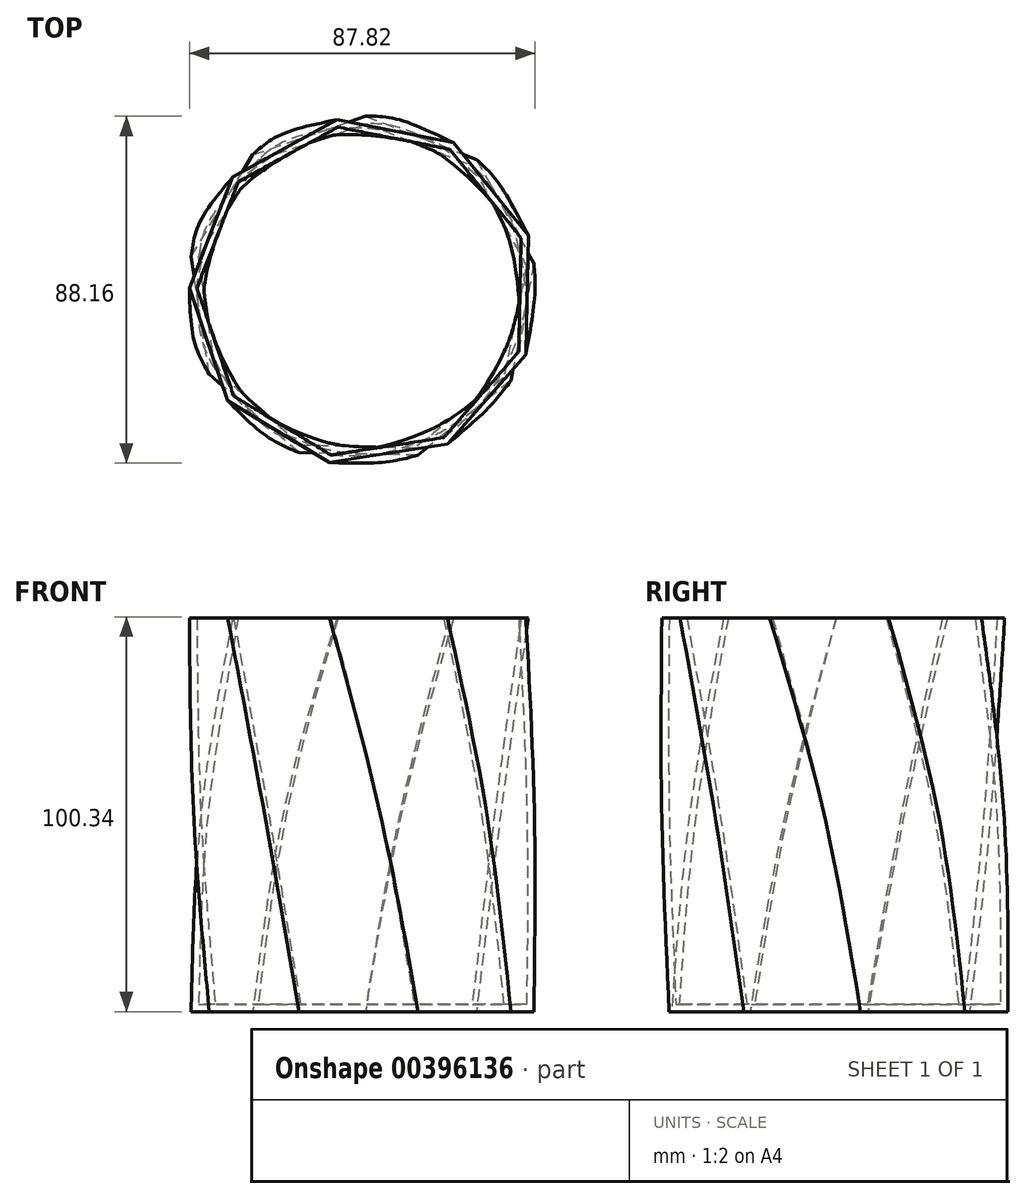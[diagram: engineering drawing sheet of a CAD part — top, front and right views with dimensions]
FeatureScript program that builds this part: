
annotation { "Feature Type Name" : "Feature", "Feature Type Description" : "" }
export const myFeature = defineFeature(function(context is Context, id is Id, definition is map)
    precondition{}
    {
        {
            var Q0;
            Q0=qCreatedBy(makeId("Top.planeOp"),FACE);
            var sketch = newSketch(context, id + "F0", { "sketchPlane" : qUnion([Q0])});
            skCircle(sketch, "E0.cCircle", {"center": v(0, 0) * mm, "radius": 41.56 * mm, "construction": true});
            skLineSegment(sketch, "E0.0", {"start": v(43.7, 6.78) * mm, "end": v(37.84, -22.9) * mm});
            skLineSegment(sketch, "E0.1", {"start": v(37.84, -22.9) * mm, "end": v(14.26, -41.87) * mm});
            skLineSegment(sketch, "E0.2", {"start": v(14.26, -41.87) * mm, "end": v(-15.98, -41.24) * mm});
            skLineSegment(sketch, "E0.3", {"start": v(-15.98, -41.24) * mm, "end": v(-38.75, -21.32) * mm});
            skLineSegment(sketch, "E0.4", {"start": v(-38.75, -21.32) * mm, "end": v(-43.39, 8.58) * mm});
            skLineSegment(sketch, "E0.5", {"start": v(-43.39, 8.58) * mm, "end": v(-27.72, 34.46) * mm});
            skLineSegment(sketch, "E0.6", {"start": v(-27.72, 34.46) * mm, "end": v(0.92, 44.22) * mm});
            skLineSegment(sketch, "E0.7", {"start": v(0.92, 44.22) * mm, "end": v(29.12, 33.29) * mm});
            skLineSegment(sketch, "E0.8", {"start": v(29.12, 33.29) * mm, "end": v(43.7, 6.78) * mm});
            skPoint(sketch, "E0.0.midPoint", {"position": v(40.77, -8.06) * mm});
            skSolve(sketch);
        }
        {
            var Q0;
            Q0=qCreatedBy(makeId("Top.planeOp"),FACE);
            cPlane(context, id + "F1", {"entities" : qUnion([Q0]), "cplaneType" : CPlaneType.OFFSET, "offset" : 50 * mm, "width" : 152.4 * mm, "height" : 152.4 * mm});
        }
        {
            var Q0;
            Q0=qCreatedBy(makeId("Top.planeOp"),FACE);
            cPlane(context, id + "F2", {"entities" : qUnion([Q0]), "cplaneType" : CPlaneType.OFFSET, "offset" : 100 * mm, "width" : 152.4 * mm, "height" : 152.4 * mm});
        }
        {
            var Q0;
            Q0=qCreatedBy(id+"F1.planeOp",FACE);
            var sketch = newSketch(context, id + "F3", { "sketchPlane" : qUnion([Q0])});
            skLineSegment(sketch, "E1.0", {"start": v(35.23, 26.53) * mm, "end": v(43.84, -2.48) * mm});
            skLineSegment(sketch, "E1.1", {"start": v(43.84, -2.48) * mm, "end": v(31.79, -30.23) * mm});
            skLineSegment(sketch, "E1.2", {"start": v(31.79, -30.23) * mm, "end": v(4.72, -43.74) * mm});
            skLineSegment(sketch, "E1.3", {"start": v(4.72, -43.74) * mm, "end": v(-24.7, -36.69) * mm});
            skLineSegment(sketch, "E1.4", {"start": v(-24.7, -36.69) * mm, "end": v(-42.7, -12.38) * mm});
            skLineSegment(sketch, "E1.5", {"start": v(-42.7, -12.38) * mm, "end": v(-40.88, 17.82) * mm});
            skLineSegment(sketch, "E1.6", {"start": v(-40.88, 17.82) * mm, "end": v(-20.06, 39.78) * mm});
            skLineSegment(sketch, "E1.7", {"start": v(-20.06, 39.78) * mm, "end": v(10, 43.21) * mm});
            skLineSegment(sketch, "E1.8", {"start": v(10, 43.21) * mm, "end": v(35.23, 26.53) * mm});
            skSolve(sketch);
        }
        {
            var Q0;
            Q0=qCreatedBy(id+"F2.planeOp",FACE);
            var sketch = newSketch(context, id + "F4", { "sketchPlane" : qUnion([Q0])});
            skLineSegment(sketch, "E2.0", {"start": v(42.29, 13.91) * mm, "end": v(41.64, -16.34) * mm});
            skLineSegment(sketch, "E2.1", {"start": v(41.64, -16.34) * mm, "end": v(21.71, -39.1) * mm});
            skLineSegment(sketch, "E2.2", {"start": v(21.71, -39.1) * mm, "end": v(-8.19, -43.72) * mm});
            skLineSegment(sketch, "E2.3", {"start": v(-8.19, -43.72) * mm, "end": v(-34.06, -28.04) * mm});
            skLineSegment(sketch, "E2.4", {"start": v(-34.06, -28.04) * mm, "end": v(-43.8, 0.6) * mm});
            skLineSegment(sketch, "E2.5", {"start": v(-43.8, 0.6) * mm, "end": v(-32.86, 28.8) * mm});
            skLineSegment(sketch, "E2.6", {"start": v(-32.86, 28.8) * mm, "end": v(-6.34, 43.38) * mm});
            skLineSegment(sketch, "E2.7", {"start": v(-6.34, 43.38) * mm, "end": v(23.33, 37.5) * mm});
            skLineSegment(sketch, "E2.8", {"start": v(23.33, 37.5) * mm, "end": v(42.29, 13.91) * mm});
            skSolve(sketch);
        }
        {
            var Q0;
            Q0=makeQuery(id+"F4.imprint","IMPRINT",FACE,{"disambiguationData":[TD([[makeQuery(id+"F4.imprint","IMPRINT",EDGE,{"derivedFrom":sQuery(id+"F4.wireOp",EDGE,"E2.0")}),-1.0]])]});
            var Q1;
            Q1=makeQuery(id+"F3.imprint","IMPRINT",FACE,{"disambiguationData":[TD([[makeQuery(id+"F3.imprint","IMPRINT",EDGE,{"derivedFrom":sQuery(id+"F3.wireOp",EDGE,"E1.0")}),-1.0]])]});
            var Q2;
            Q2=makeQuery(id+"F0.imprint","IMPRINT",FACE,{"disambiguationData":[TD([[makeQuery(id+"F0.imprint","IMPRINT",EDGE,{"derivedFrom":sQuery(id+"F0.wireOp",EDGE,"E0.0")}),-1.0]])]});
            loft(context, id + "F5", {"sheetProfilesArray" : [{ "sheetProfileEntities" : qUnion([Q0]) }, { "sheetProfileEntities" : qUnion([Q1]) }, { "sheetProfileEntities" : qUnion([Q2]) }]});
        }
        {
            var Q0;
            Q0=makeQuery(id+"F5.opLoft","CAP_FACE",FACE,{"disambiguationData":[OSD([makeQuery(id+"F4.imprint","IMPRINT",FACE,{"disambiguationData":[TD([[makeQuery(id+"F4.imprint","IMPRINT",EDGE,{"derivedFrom":sQuery(id+"F4.wireOp",EDGE,"E2.0")}),-1.0]])]})])],"isStart":true});
            shell(context, id + "F6", {"entities" : qUnion([Q0]), "thickness" : 1.8 * mm});
        }
    });
